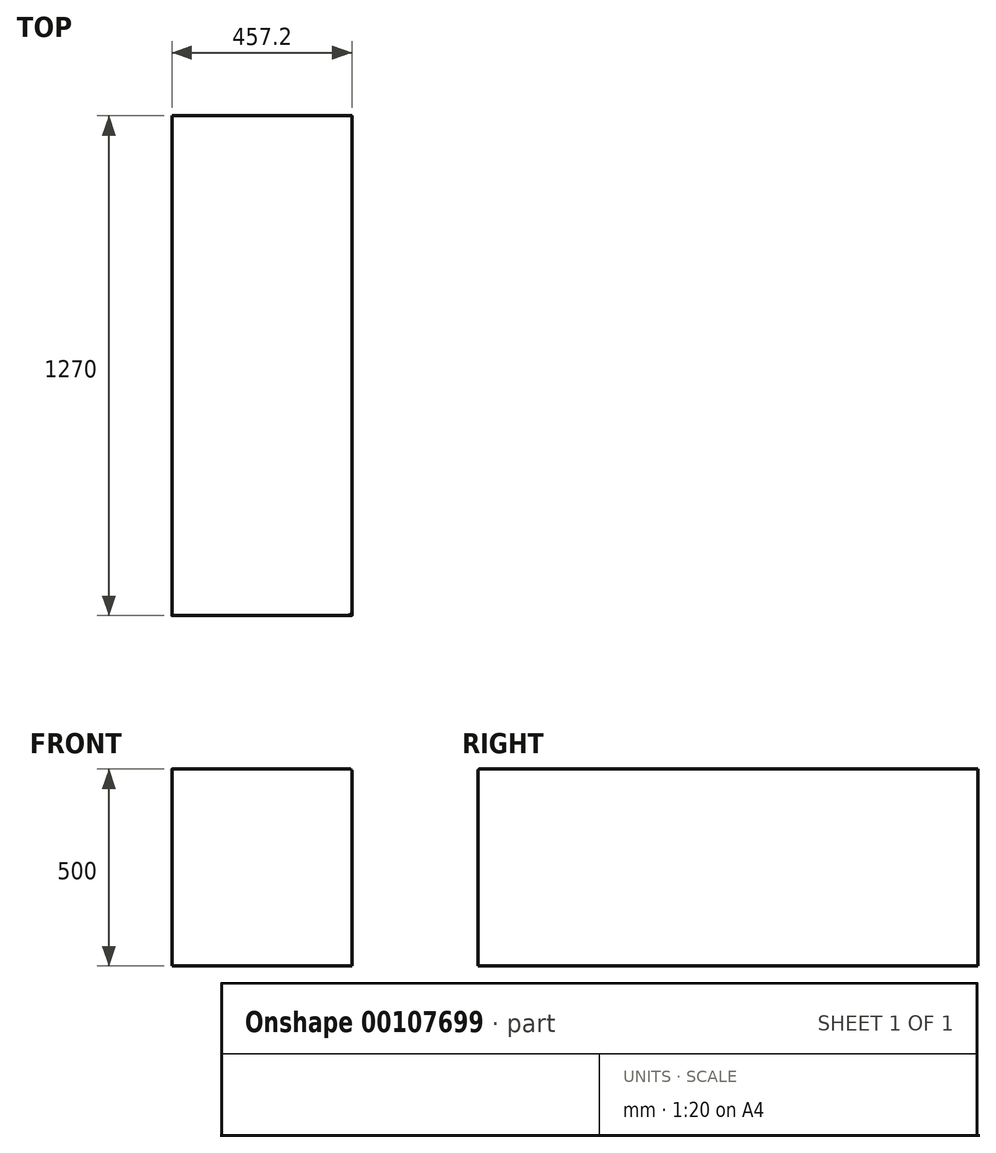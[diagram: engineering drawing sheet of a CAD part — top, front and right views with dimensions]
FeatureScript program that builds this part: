
annotation { "Feature Type Name" : "Feature", "Feature Type Description" : "" }
export const myFeature = defineFeature(function(context is Context, id is Id, definition is map)
    precondition{}
    {
        {
            var Q0;
            Q0=qCreatedBy(makeId("Front.planeOp"),FACE);
            var sketch = newSketch(context, id + "F0", { "sketchPlane" : qUnion([Q0])});
            skLineSegment(sketch, "E0.bottom", {"start": v(-228.6, 250) * mm, "end": v(228.6, 250) * mm});
            skLineSegment(sketch, "E0.top", {"start": v(-228.6, -250) * mm, "end": v(228.6, -250) * mm});
            skLineSegment(sketch, "E0.left", {"start": v(-228.6, 250) * mm, "end": v(-228.6, -250) * mm});
            skLineSegment(sketch, "E0.right", {"start": v(228.6, 250) * mm, "end": v(228.6, -250) * mm});
            skPoint(sketch, "E0.middle", {"position": v(0, 0) * mm});
            skSolve(sketch);
        }
        {
            var Q0;
            Q0=makeQuery(id+"F0.imprint","IMPRINT",FACE,{"disambiguationData":[TD([[makeQuery(id+"F0.imprint","IMPRINT",EDGE,{"derivedFrom":sQuery(id+"F0.wireOp",EDGE,"E0.bottom")}),-1.0]])]});
            extrude(context, id + "F1", {"entities" : qUnion([Q0]), "endBound" : BoundingType.SYMMETRIC, "depth" : 1270 * mm});
        }
        {
            var Q0;
            Q0=makeQuery(id+"F1.opExtrude","CAP_EDGE",EDGE,{"disambiguationData":[OSD([sQuery(id+"F0.wireOp",EDGE,"E0.bottom")])],"isStart":false});
            var Q1;
            Q1=makeQuery(id+"F1.opExtrude","SWEPT_EDGE",EDGE,{"disambiguationData":[OSD([sQuery(id+"F0.wireOp",EDGE,"E0.bottom"),sQuery(id+"F0.wireOp",EDGE,"E0.right")])]});
            fillet(context, id + "F2", {"entities" : qUnion([Q0, Q1]), "radius" : 5.08 * mm, "tangentPropagation" : true, "allowEdgeOverflow" : false});
        }
    });
